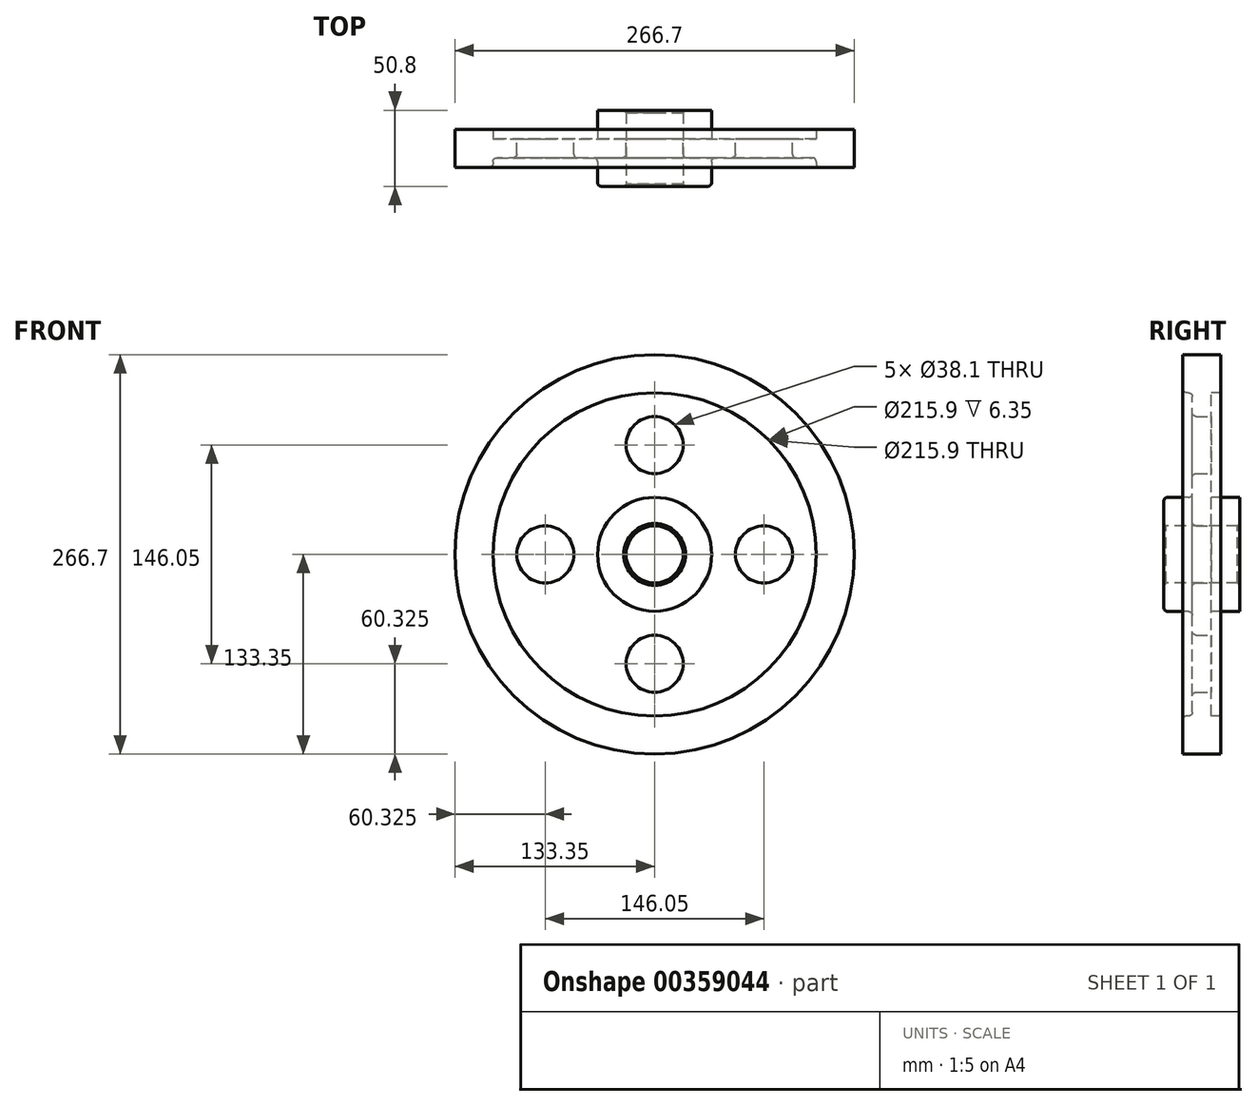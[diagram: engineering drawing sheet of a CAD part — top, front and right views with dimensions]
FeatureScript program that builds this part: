
annotation { "Feature Type Name" : "Feature", "Feature Type Description" : "" }
export const myFeature = defineFeature(function(context is Context, id is Id, definition is map)
    precondition{}
    {
        {
            var Q0;
            Q0=qCreatedBy(makeId("Right.planeOp"),FACE);
            var sketch = newSketch(context, id + "F0", { "sketchPlane" : qUnion([Q0])});
            skLineSegment(sketch, "E0", {"start": v(0, 0) * mm, "end": v(0, 28.58) * mm});
            skLineSegment(sketch, "E1", {"start": v(0, 28.58) * mm, "end": v(0, 0) * mm});
            skLineSegment(sketch, "E2", {"start": v(0, 28.58) * mm, "end": v(0, 73.03) * mm});
            skLineSegment(sketch, "E3", {"start": v(0, 73.03) * mm, "end": v(0, 120.65) * mm});
            skLineSegment(sketch, "E4.bottom", {"start": v(25.4, 19.05) * mm, "end": v(-25.4, 19.05) * mm});
            skLineSegment(sketch, "E4.top", {"start": v(25.4, 38.1) * mm, "end": v(6.35, 38.1) * mm});
            skLineSegment(sketch, "E4.left", {"start": v(25.4, 19.05) * mm, "end": v(25.4, 38.1) * mm});
            skLineSegment(sketch, "E4.right", {"start": v(-25.4, 19.05) * mm, "end": v(-25.4, 38.1) * mm});
            skPoint(sketch, "E4.middle", {"position": v(0, 28.58) * mm});
            skLineSegment(sketch, "E5.bottom", {"start": v(12.7, 133.35) * mm, "end": v(-12.7, 133.35) * mm});
            skLineSegment(sketch, "E5.top", {"start": v(12.7, 107.95) * mm, "end": v(6.35, 107.95) * mm});
            skLineSegment(sketch, "E5.left", {"start": v(12.7, 133.35) * mm, "end": v(12.7, 107.95) * mm});
            skLineSegment(sketch, "E5.right", {"start": v(-12.7, 133.35) * mm, "end": v(-12.7, 107.95) * mm});
            skPoint(sketch, "E5.middle", {"position": v(0, 120.65) * mm});
            skLineSegment(sketch, "E6.left", {"start": v(6.35, 28.58) * mm, "end": v(6.35, 117.48) * mm});
            skLineSegment(sketch, "E6.right", {"start": v(-6.35, 28.58) * mm, "end": v(-6.35, 117.48) * mm});
            skPoint(sketch, "E6.middle", {"position": v(0, 73.03) * mm});
            skLineSegment(sketch, "E7.trimOffspring", {"start": v(-6.35, 107.95) * mm, "end": v(-12.7, 107.95) * mm});
            skLineSegment(sketch, "E8.trimOffspring", {"start": v(-6.35, 38.1) * mm, "end": v(-25.4, 38.1) * mm});
            skLineSegment(sketch, "E9", {"start": v(0, 0) * mm, "end": v(14.88, 0) * mm});
            skSolve(sketch);
        }
        {
            var Q0;
            {var subQ4=sQuery(id+"F0.wireOp",EDGE,"E4.top");Q0=makeQuery(id+"F0.imprint","IMPRINT",FACE,{"disambiguationData":[TD([[makeQuery(id+"F0.imprint","IMPRINT",EDGE,{"derivedFrom":subQ4}),1.0]])]});}
            var Q1;
            Q1=sQuery(id+"F0.wireOp",EDGE,"E9");
            revolve(context, id + "F1", {"entities" : qUnion([Q0]), "axis" : qUnion([Q1]), "revolveType" : RevolveType.FULL});
        }
        {
            var Q0;
            Q0=makeQuery(id+"F1.opRevolve","SWEPT_FACE",FACE,{"disambiguationData":[OSD([sQuery(id+"F0.wireOp",EDGE,"E6.left")])]});
            var sketch = newSketch(context, id + "F2", { "sketchPlane" : qUnion([Q0])});
            skLineSegment(sketch, "E10", {"start": v(0, 0) * mm, "end": v(0, 3.97) * mm});
            skLineSegment(sketch, "E11", {"start": v(0, 0) * mm, "end": v(0, 73.03) * mm});
            skPoint(sketch, "E11.endSnap0", {"position": v(0, 1.98) * mm});
            skCircle(sketch, "E12", {"center": v(0, 73.03) * mm, "radius": 19.05 * mm});
            skCircle(sketch, "E13.1.0", {"center": v(-73.03, 0) * mm, "radius": 19.05 * mm});
            skCircle(sketch, "E13.2.0", {"center": v(0, -73.03) * mm, "radius": 19.05 * mm});
            skCircle(sketch, "E13.3.0", {"center": v(73.03, 0) * mm, "radius": 19.05 * mm});
            skPoint(sketch, "E13.center", {"position": v(0, 0) * mm});
            skSolve(sketch);
        }
        {
            var Q0;
            Q0=makeQuery(id+"F2.imprint","IMPRINT",FACE,{"disambiguationData":[TD([[makeQuery(id+"F2.imprint","IMPRINT",EDGE,{"derivedFrom":sQuery(id+"F2.wireOp",EDGE,"E12")}),1.0]])]});
            var Q1;
            Q1=makeQuery(id+"F2.imprint","IMPRINT",FACE,{"disambiguationData":[TD([[makeQuery(id+"F2.imprint","IMPRINT",EDGE,{"derivedFrom":sQuery(id+"F2.wireOp",EDGE,"E13.1.0")}),1.0]])]});
            var Q2;
            Q2=makeQuery(id+"F2.imprint","IMPRINT",FACE,{"disambiguationData":[TD([[makeQuery(id+"F2.imprint","IMPRINT",EDGE,{"derivedFrom":sQuery(id+"F2.wireOp",EDGE,"E13.3.0")}),1.0]])]});
            var Q3;
            Q3=makeQuery(id+"F2.imprint","IMPRINT",FACE,{"disambiguationData":[TD([[makeQuery(id+"F2.imprint","IMPRINT",EDGE,{"derivedFrom":sQuery(id+"F2.wireOp",EDGE,"E13.2.0")}),1.0]])]});
            extrude(context, id + "F3", {"entities" : qUnion([Q0, Q1, Q2, Q3]), "operationType" : NewBodyOperationType.REMOVE, "oppositeDirection" : true, "depth" : 25.4 * mm});
        }
        {
            var Q0;
            Q0=makeQuery(id+"F1.opRevolve","SWEPT_FACE",FACE,{"disambiguationData":[OSD([sQuery(id+"F0.wireOp",EDGE,"E6.right")])]});
            var Q1;
            Q1=makeQuery(id+"F1.opRevolve","SWEPT_EDGE",EDGE,{"disambiguationData":[OSD([sQuery(id+"F0.wireOp",EDGE,"E6.right"),sQuery(id+"F0.wireOp",EDGE,"E7.trimOffspring")])]});
            var Q2;
            Q2=makeQuery(id+"F1.opRevolve","SWEPT_EDGE",EDGE,{"disambiguationData":[OSD([sQuery(id+"F0.wireOp",EDGE,"E5.right"),sQuery(id+"F0.wireOp",EDGE,"E7.trimOffspring")])]});
            var Q3;
            Q3=makeQuery(id+"F1.opRevolve","SWEPT_EDGE",EDGE,{"disambiguationData":[OSD([sQuery(id+"F0.wireOp",EDGE,"E6.right"),sQuery(id+"F0.wireOp",EDGE,"E8.trimOffspring")])]});
            var Q4;
            Q4=makeQuery(id+"F1.opRevolve","SWEPT_FACE",FACE,{"disambiguationData":[OSD([sQuery(id+"F0.wireOp",EDGE,"E8.trimOffspring")])]});
            fillet(context, id + "F4", {"entities" : qUnion([Q0, Q1, Q2, Q3, Q4]), "radius" : 2.54 * mm, "tangentPropagation" : true, "allowEdgeOverflow" : false});
        }
        {
            var Q0;
            Q0=makeQuery(id+"F1.opRevolve","SWEPT_EDGE",EDGE,{"disambiguationData":[OSD([sQuery(id+"F0.wireOp",EDGE,"E4.bottom"),sQuery(id+"F0.wireOp",EDGE,"E4.right")])]});
            var Q1;
            Q1=makeQuery(id+"F1.opRevolve","SWEPT_EDGE",EDGE,{"disambiguationData":[OSD([sQuery(id+"F0.wireOp",EDGE,"E4.bottom"),sQuery(id+"F0.wireOp",EDGE,"E4.left")])]});
            chamfer(context, id + "F5", {"entities" : qUnion([Q0, Q1]), "width" : 1.59 * mm, "tangentPropagation" : true});
        }
    });
